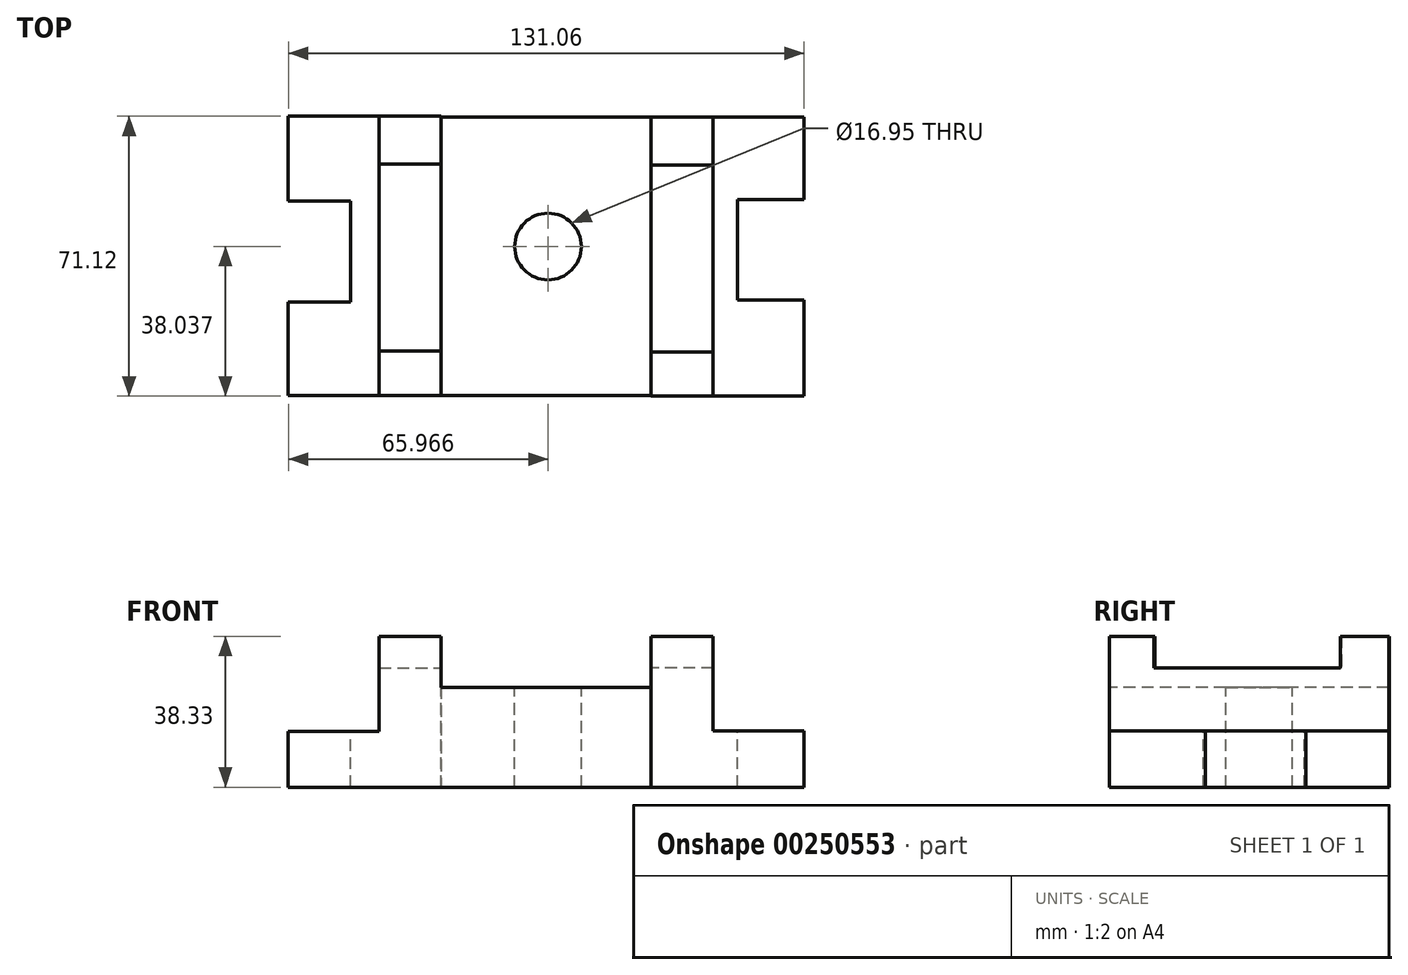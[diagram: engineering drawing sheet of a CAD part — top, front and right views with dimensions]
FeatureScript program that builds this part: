
annotation { "Feature Type Name" : "Feature", "Feature Type Description" : "" }
export const myFeature = defineFeature(function(context is Context, id is Id, definition is map)
    precondition{}
    {
        {
            var Q0;
            Q0=qCreatedBy(makeId("Top.planeOp"),FACE);
            var sketch = newSketch(context, id + "F0", { "sketchPlane" : qUnion([Q0])});
            skLineSegment(sketch, "E0.bottom", {"start": v(-31.77, 25.5) * mm, "end": v(21.57, 25.5) * mm});
            skLineSegment(sketch, "E0.top", {"start": v(-31.77, -45.32) * mm, "end": v(21.57, -45.32) * mm});
            skLineSegment(sketch, "E0.left", {"start": v(-31.77, 25.5) * mm, "end": v(-31.77, -45.32) * mm});
            skLineSegment(sketch, "E0.right", {"start": v(21.57, 25.5) * mm, "end": v(21.57, -45.32) * mm});
            skSolve(sketch);
        }
        {
            var Q0;
            Q0 = qSketchRegion(id + "F0", true);
            extrude(context, id + "F1", {"entities" : qUnion([Q0]), "depth" : 25.4 * mm});
        }
        {
            var Q0;
            Q0=makeQuery(id+"F1.opExtrude","CAP_FACE",FACE,{"disambiguationData":[OSD([sQuery(id+"F0.wireOp",EDGE,"E0.bottom"),sQuery(id+"F0.wireOp",EDGE,"E0.top"),sQuery(id+"F0.wireOp",EDGE,"E0.left"),sQuery(id+"F0.wireOp",EDGE,"E0.right")])],"isStart":false});
            var sketch = newSketch(context, id + "F2", { "sketchPlane" : qUnion([Q0])});
            skCircle(sketch, "E1", {"center": v(-4.66, -7.43) * mm, "radius": 8.47 * mm});
            skSolve(sketch);
        }
        {
            var Q0;
            Q0 = qSketchRegion(id + "F2", true);
            extrude(context, id + "F3", {"entities" : qUnion([Q0]), "operationType" : NewBodyOperationType.REMOVE, "oppositeDirection" : true, "depth" : 41.4 * mm});
        }
        {
            var Q0;
            Q0=makeQuery(id+"F1.opExtrude","SWEPT_FACE",FACE,{"disambiguationData":[OSD([sQuery(id+"F0.wireOp",EDGE,"E0.left")])]});
            var sketch = newSketch(context, id + "F4", { "sketchPlane" : qUnion([Q0])});
            skLineSegment(sketch, "E2.bottom", {"start": v(45.32, 0) * mm, "end": v(-25.65, 0) * mm});
            skLineSegment(sketch, "E2.top", {"start": v(45.32, 38.33) * mm, "end": v(-25.65, 38.33) * mm});
            skLineSegment(sketch, "E2.left", {"start": v(45.32, 0) * mm, "end": v(45.32, 38.33) * mm});
            skLineSegment(sketch, "E2.right", {"start": v(-25.65, 0) * mm, "end": v(-25.65, 38.33) * mm});
            skSolve(sketch);
        }
        {
            var Q0;
            Q0 = qSketchRegion(id + "F4", true);
            extrude(context, id + "F5", {"entities" : qUnion([Q0]), "operationType" : NewBodyOperationType.ADD, "depth" : 15.75 * mm});
        }
        {
            var Q0;
            Q0=makeQuery(id+"F1.opExtrude","SWEPT_FACE",FACE,{"disambiguationData":[OSD([sQuery(id+"F0.wireOp",EDGE,"E0.right")])]});
            var sketch = newSketch(context, id + "F6", { "sketchPlane" : qUnion([Q0])});
            skLineSegment(sketch, "E3.bottom", {"start": v(25.5, 0) * mm, "end": v(-45.47, 0) * mm});
            skLineSegment(sketch, "E3.top", {"start": v(25.5, 38.33) * mm, "end": v(-45.47, 38.33) * mm});
            skLineSegment(sketch, "E3.left", {"start": v(25.5, 0) * mm, "end": v(25.5, 38.33) * mm});
            skLineSegment(sketch, "E3.right", {"start": v(-45.47, 0) * mm, "end": v(-45.47, 38.33) * mm});
            skSolve(sketch);
        }
        {
            var Q0;
            Q0 = qSketchRegion(id + "F6", true);
            extrude(context, id + "F7", {"entities" : qUnion([Q0]), "operationType" : NewBodyOperationType.ADD, "depth" : 15.75 * mm});
        }
        {
            var Q0;
            Q0=makeQuery(id+"F5.opExtrude","CAP_FACE",FACE,{"disambiguationData":[OSD([sQuery(id+"F4.wireOp",EDGE,"E2.bottom"),sQuery(id+"F4.wireOp",EDGE,"E2.top"),sQuery(id+"F4.wireOp",EDGE,"E2.left"),sQuery(id+"F4.wireOp",EDGE,"E2.right")])],"isStart":false});
            var sketch = newSketch(context, id + "F8", { "sketchPlane" : qUnion([Q0])});
            skLineSegment(sketch, "E4", {"start": v(-25.65, 0) * mm, "end": v(-25.65, 14.14) * mm});
            skLineSegment(sketch, "E5", {"start": v(-25.65, 14.14) * mm, "end": v(45.32, 14.14) * mm});
            skLineSegment(sketch, "E6", {"start": v(45.32, 14.14) * mm, "end": v(45.32, 0) * mm});
            skLineSegment(sketch, "E7", {"start": v(45.32, 0) * mm, "end": v(-25.65, 0) * mm});
            skSolve(sketch);
        }
        {
            var Q0;
            Q0 = qSketchRegion(id + "F8", true);
            extrude(context, id + "F9", {"entities" : qUnion([Q0]), "operationType" : NewBodyOperationType.ADD, "depth" : 23.1 * mm});
        }
        {
            var Q0;
            Q0=makeQuery(id+"F7.opExtrude","CAP_FACE",FACE,{"disambiguationData":[OSD([sQuery(id+"F6.wireOp",EDGE,"E3.bottom"),sQuery(id+"F6.wireOp",EDGE,"E3.top"),sQuery(id+"F6.wireOp",EDGE,"E3.left"),sQuery(id+"F6.wireOp",EDGE,"E3.right")])],"isStart":false});
            var sketch = newSketch(context, id + "F10", { "sketchPlane" : qUnion([Q0])});
            skLineSegment(sketch, "E8", {"start": v(-45.47, 0) * mm, "end": v(25.5, 0) * mm});
            skLineSegment(sketch, "E9", {"start": v(25.5, 0) * mm, "end": v(25.5, 14.34) * mm});
            skLineSegment(sketch, "E10", {"start": v(25.5, 14.34) * mm, "end": v(-45.47, 14.34) * mm});
            skLineSegment(sketch, "E11", {"start": v(-45.47, 14.34) * mm, "end": v(-45.47, 0) * mm});
            skSolve(sketch);
        }
        {
            var Q0;
            Q0 = qSketchRegion(id + "F10", true);
            extrude(context, id + "F11", {"entities" : qUnion([Q0]), "operationType" : NewBodyOperationType.ADD, "depth" : 23.1 * mm});
        }
        {
            var Q0;
            Q0=makeQuery(id+"F11.opExtrude","SWEPT_FACE",FACE,{"disambiguationData":[OSD([sQuery(id+"F10.wireOp",EDGE,"E10")])]});
            var sketch = newSketch(context, id + "F12", { "sketchPlane" : qUnion([Q0])});
            skLineSegment(sketch, "E12.bottom", {"start": v(60.43, -21.04) * mm, "end": v(43.44, -21.04) * mm});
            skLineSegment(sketch, "E12.top", {"start": v(60.43, 4.44) * mm, "end": v(43.44, 4.44) * mm});
            skLineSegment(sketch, "E12.left", {"start": v(60.43, -21.04) * mm, "end": v(60.43, 4.44) * mm});
            skLineSegment(sketch, "E12.right", {"start": v(43.44, -21.04) * mm, "end": v(43.44, 4.44) * mm});
            skSolve(sketch);
        }
        {
            var Q0;
            Q0 = qSketchRegion(id + "F12", true);
            extrude(context, id + "F13", {"entities" : qUnion([Q0]), "operationType" : NewBodyOperationType.REMOVE, "oppositeDirection" : true, "depth" : 25.4 * mm});
        }
        {
            var Q0;
            Q0=makeQuery(id+"F9.opExtrude","SWEPT_FACE",FACE,{"disambiguationData":[OSD([sQuery(id+"F8.wireOp",EDGE,"E5")])]});
            var sketch = newSketch(context, id + "F14", { "sketchPlane" : qUnion([Q0])});
            skLineSegment(sketch, "E13.bottom", {"start": v(-70.63, 4.08) * mm, "end": v(-54.77, 4.08) * mm});
            skLineSegment(sketch, "E13.top", {"start": v(-70.63, -21.57) * mm, "end": v(-54.77, -21.57) * mm});
            skLineSegment(sketch, "E13.left", {"start": v(-70.63, 4.08) * mm, "end": v(-70.63, -21.57) * mm});
            skLineSegment(sketch, "E13.right", {"start": v(-54.77, 4.08) * mm, "end": v(-54.77, -21.57) * mm});
            skSolve(sketch);
        }
        {
            var Q0;
            Q0 = qSketchRegion(id + "F14", true);
            extrude(context, id + "F15", {"entities" : qUnion([Q0]), "operationType" : NewBodyOperationType.REMOVE, "oppositeDirection" : true, "depth" : 25.4 * mm});
        }
        {
            var Q0;
            Q0=makeQuery(id+"F7.opExtrude","CAP_FACE",FACE,{"disambiguationData":[OSD([sQuery(id+"F6.wireOp",EDGE,"E3.bottom"),sQuery(id+"F6.wireOp",EDGE,"E3.top"),sQuery(id+"F6.wireOp",EDGE,"E3.left"),sQuery(id+"F6.wireOp",EDGE,"E3.right")])],"isStart":true});
            var sketch = newSketch(context, id + "F16", { "sketchPlane" : qUnion([Q0])});
            skLineSegment(sketch, "E14.bottom", {"start": v(-13.23, 38.33) * mm, "end": v(34.2, 38.33) * mm});
            skLineSegment(sketch, "E14.top", {"start": v(-13.23, 30.33) * mm, "end": v(34.2, 30.33) * mm});
            skLineSegment(sketch, "E14.left", {"start": v(-13.23, 38.33) * mm, "end": v(-13.23, 30.33) * mm});
            skLineSegment(sketch, "E14.right", {"start": v(34.2, 38.33) * mm, "end": v(34.2, 30.33) * mm});
            skSolve(sketch);
        }
        {
            var Q0;
            Q0 = qSketchRegion(id + "F16", true);
            extrude(context, id + "F17", {"entities" : qUnion([Q0]), "operationType" : NewBodyOperationType.REMOVE, "oppositeDirection" : true, "depth" : 25.4 * mm});
        }
        {
            var Q0;
            Q0=makeQuery(id+"F5.opExtrude","CAP_FACE",FACE,{"disambiguationData":[OSD([sQuery(id+"F4.wireOp",EDGE,"E2.bottom"),sQuery(id+"F4.wireOp",EDGE,"E2.top"),sQuery(id+"F4.wireOp",EDGE,"E2.left"),sQuery(id+"F4.wireOp",EDGE,"E2.right")])],"isStart":true});
            var sketch = newSketch(context, id + "F18", { "sketchPlane" : qUnion([Q0])});
            skLineSegment(sketch, "E15.bottom", {"start": v(-33.95, 38.33) * mm, "end": v(13.48, 38.33) * mm});
            skLineSegment(sketch, "E15.top", {"start": v(-33.95, 30.33) * mm, "end": v(13.48, 30.33) * mm});
            skLineSegment(sketch, "E15.left", {"start": v(-33.95, 38.33) * mm, "end": v(-33.95, 30.33) * mm});
            skLineSegment(sketch, "E15.right", {"start": v(13.48, 38.33) * mm, "end": v(13.48, 30.33) * mm});
            skSolve(sketch);
        }
        {
            var Q0;
            Q0 = qSketchRegion(id + "F18", true);
            extrude(context, id + "F19", {"entities" : qUnion([Q0]), "operationType" : NewBodyOperationType.REMOVE, "oppositeDirection" : true, "depth" : 25.4 * mm});
        }
    });
